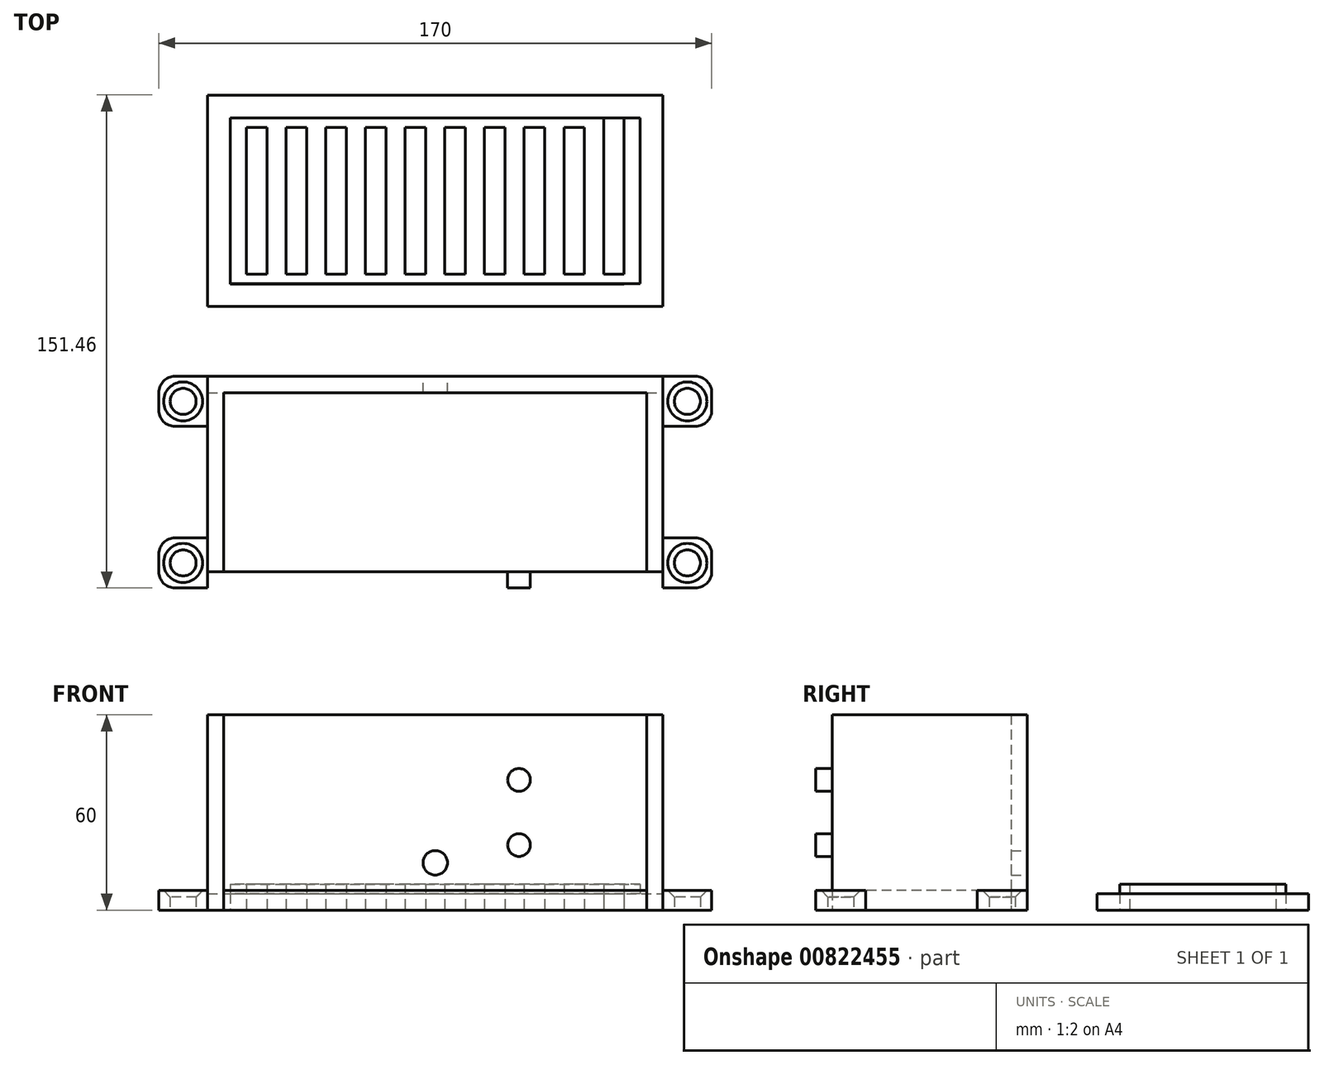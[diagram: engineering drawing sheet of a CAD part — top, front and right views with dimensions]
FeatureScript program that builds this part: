
annotation { "Feature Type Name" : "Feature", "Feature Type Description" : "" }
export const myFeature = defineFeature(function(context is Context, id is Id, definition is map)
    precondition{}
    {
        {
            var Q0;
            Q0=qCreatedBy(makeId("Top.planeOp"),FACE);
            var sketch = newSketch(context, id + "F0", { "sketchPlane" : qUnion([Q0])});
            skLineSegment(sketch, "E0.bottom", {"start": v(-70, 32.5) * mm, "end": v(70, 32.5) * mm});
            skLineSegment(sketch, "E0.top", {"start": v(-70, -32.5) * mm, "end": v(70, -32.5) * mm});
            skLineSegment(sketch, "E0.left", {"start": v(-70, 32.5) * mm, "end": v(-70, -32.5) * mm});
            skLineSegment(sketch, "E0.right", {"start": v(70, 32.5) * mm, "end": v(70, -32.5) * mm});
            skPoint(sketch, "E0.middle", {"position": v(0, 0) * mm});
            skLineSegment(sketch, "E1", {"start": v(70, -32.5) * mm, "end": v(80, -32.5) * mm});
            skCircle(sketch, "E2", {"center": v(77.5, -24.82) * mm, "radius": 4 * mm});
            skLineSegment(sketch, "E3", {"start": v(85, -27.5) * mm, "end": v(85, -22.13) * mm});
            skLineSegment(sketch, "E4", {"start": v(80, -17.13) * mm, "end": v(70, -17.13) * mm});
            skLineSegment(sketch, "E5", {"start": v(77.5, -32.5) * mm, "end": v(77.5, -17.13) * mm, "construction": true});
            skLineSegment(sketch, "E6", {"start": v(85, -24.82) * mm, "end": v(70, -24.82) * mm, "construction": true});
            skLineSegment(sketch, "E7.MirrorCS", {"start": v(80, 17.13) * mm, "end": v(70, 17.13) * mm});
            skCircle(sketch, "E8.MirrorC", {"center": v(77.5, 24.82) * mm, "radius": 4 * mm});
            skLineSegment(sketch, "E9.MirrorCS", {"start": v(85, 27.5) * mm, "end": v(85, 22.13) * mm});
            skLineSegment(sketch, "E10.MirrorCS", {"start": v(70, 32.5) * mm, "end": v(80, 32.5) * mm});
            skLineSegment(sketch, "E11.MirrorCS", {"start": v(-70, 32.5) * mm, "end": v(-80, 32.5) * mm});
            skLineSegment(sketch, "E12.MirrorCS", {"start": v(-80, 17.13) * mm, "end": v(-70, 17.13) * mm});
            skLineSegment(sketch, "E13.MirrorCS", {"start": v(-85, 27.5) * mm, "end": v(-85, 22.13) * mm});
            skCircle(sketch, "E14.MirrorC", {"center": v(-77.5, 24.82) * mm, "radius": 4 * mm});
            skLineSegment(sketch, "E15.MirrorCS", {"start": v(-80, -17.13) * mm, "end": v(-70, -17.13) * mm});
            skLineSegment(sketch, "E16.MirrorCS", {"start": v(-85, -27.5) * mm, "end": v(-85, -22.13) * mm});
            skLineSegment(sketch, "E17.MirrorCS", {"start": v(-70, -32.5) * mm, "end": v(-80, -32.5) * mm});
            skCircle(sketch, "E18.MirrorC", {"center": v(-77.5, -24.82) * mm, "radius": 4 * mm});
            skPoint(sketch, "E19.visualSharp", {"position": v(85, -17.13) * mm});
            skArc(sketch, "E19.filletArc", {"start": v(85, -22.13) * mm, "mid": v(83.54, -18.6) * mm, "end": v(80, -17.13) * mm});
            skPoint(sketch, "E20.visualSharp", {"position": v(85, -32.5) * mm});
            skArc(sketch, "E20.filletArc", {"start": v(80, -32.5) * mm, "mid": v(83.54, -31.04) * mm, "end": v(85, -27.5) * mm});
            skPoint(sketch, "E21.visualSharp", {"position": v(85, 32.5) * mm});
            skArc(sketch, "E21.filletArc", {"start": v(85, 27.5) * mm, "mid": v(83.54, 31.04) * mm, "end": v(80, 32.5) * mm});
            skPoint(sketch, "E22.visualSharp", {"position": v(85, 17.13) * mm});
            skArc(sketch, "E22.filletArc", {"start": v(80, 17.13) * mm, "mid": v(83.54, 18.6) * mm, "end": v(85, 22.13) * mm});
            skPoint(sketch, "E23.visualSharp", {"position": v(-85, 32.5) * mm});
            skArc(sketch, "E23.filletArc", {"start": v(-80, 32.5) * mm, "mid": v(-83.54, 31.04) * mm, "end": v(-85, 27.5) * mm});
            skPoint(sketch, "E24.visualSharp", {"position": v(-85, 17.13) * mm});
            skArc(sketch, "E24.filletArc", {"start": v(-85, 22.13) * mm, "mid": v(-83.54, 18.6) * mm, "end": v(-80, 17.13) * mm});
            skPoint(sketch, "E25.visualSharp", {"position": v(-85, -17.13) * mm});
            skArc(sketch, "E25.filletArc", {"start": v(-80, -17.13) * mm, "mid": v(-83.54, -18.6) * mm, "end": v(-85, -22.13) * mm});
            skPoint(sketch, "E26.visualSharp", {"position": v(-85, -32.5) * mm});
            skArc(sketch, "E26.filletArc", {"start": v(-85, -27.5) * mm, "mid": v(-83.54, -31.04) * mm, "end": v(-80, -32.5) * mm});
            skLineSegment(sketch, "E27", {"start": v(-65, 32.5) * mm, "end": v(-65, -32.5) * mm});
            skLineSegment(sketch, "E28", {"start": v(-70, 27.5) * mm, "end": v(70, 27.5) * mm});
            skLineSegment(sketch, "E29", {"start": v(65, 32.5) * mm, "end": v(65, -32.5) * mm});
            skLineSegment(sketch, "E30", {"start": v(-70, -27.5) * mm, "end": v(70, -27.5) * mm});
            skLineSegment(sketch, "E31.bottom", {"start": v(-70, 118.96) * mm, "end": v(70, 118.96) * mm});
            skLineSegment(sketch, "E31.top", {"start": v(-70, 53.96) * mm, "end": v(70, 53.96) * mm});
            skLineSegment(sketch, "E31.left", {"start": v(-70, 118.96) * mm, "end": v(-70, 53.96) * mm});
            skLineSegment(sketch, "E31.right", {"start": v(70, 118.96) * mm, "end": v(70, 53.96) * mm});
            skPoint(sketch, "E31.middle", {"position": v(0, 86.46) * mm});
            skPoint(sketch, "E31.middle.positionSnap0", {"position": v(0, -32.5) * mm});
            skPoint(sketch, "E31.centerSnap0", {"position": v(0, -32.5) * mm});
            skLineSegment(sketch, "E32", {"start": v(-63, 118.96) * mm, "end": v(-63, 53.96) * mm});
            skLineSegment(sketch, "E33", {"start": v(-70, 60.96) * mm, "end": v(70, 60.96) * mm});
            skLineSegment(sketch, "E34", {"start": v(63, 53.96) * mm, "end": v(63, 118.96) * mm});
            skLineSegment(sketch, "E35.top", {"start": v(-63, 60.91) * mm, "end": v(61.3, 60.91) * mm});
            skLineSegment(sketch, "E35.left", {"start": v(-63, 112.53) * mm, "end": v(-63, 60.91) * mm});
            skLineSegment(sketch, "E36", {"start": v(70, 111.96) * mm, "end": v(-70, 111.96) * mm});
            skLineSegment(sketch, "E37.bottom", {"start": v(58.04, 111.96) * mm, "end": v(51.74, 111.96) * mm});
            skLineSegment(sketch, "E37.top", {"start": v(58.04, 60.91) * mm, "end": v(51.74, 60.91) * mm});
            skLineSegment(sketch, "E37.left", {"start": v(58.04, 111.96) * mm, "end": v(58.04, 60.91) * mm});
            skLineSegment(sketch, "E37.right", {"start": v(51.74, 111.96) * mm, "end": v(51.74, 60.91) * mm});
            skLineSegment(sketch, "E38.1.0.0", {"start": v(39.54, 111.96) * mm, "end": v(39.54, 60.91) * mm});
            skLineSegment(sketch, "E38.1.0.1", {"start": v(45.84, 111.96) * mm, "end": v(45.84, 60.91) * mm});
            skLineSegment(sketch, "E38.2.0.0", {"start": v(27.34, 111.96) * mm, "end": v(27.34, 60.91) * mm});
            skLineSegment(sketch, "E38.2.0.1", {"start": v(33.64, 111.96) * mm, "end": v(33.64, 60.91) * mm});
            skLineSegment(sketch, "E38.direction1", {"start": v(51.74, 60.91) * mm, "end": v(39.54, 60.91) * mm, "construction": true});
            skLineSegment(sketch, "E39.0.3.0", {"start": v(15.14, 111.96) * mm, "end": v(15.14, 60.91) * mm});
            skLineSegment(sketch, "E39.3.3.0", {"start": v(21.44, 111.96) * mm, "end": v(21.44, 60.91) * mm});
            skLineSegment(sketch, "E39.0.4.0", {"start": v(2.94, 111.96) * mm, "end": v(2.94, 60.91) * mm});
            skLineSegment(sketch, "E39.3.4.0", {"start": v(9.24, 111.96) * mm, "end": v(9.24, 60.91) * mm});
            skLineSegment(sketch, "E39.0.5.0", {"start": v(-9.26, 111.96) * mm, "end": v(-9.26, 60.91) * mm});
            skLineSegment(sketch, "E39.3.5.0", {"start": v(-2.96, 111.96) * mm, "end": v(-2.96, 60.91) * mm});
            skLineSegment(sketch, "E39.0.6.0", {"start": v(-21.46, 111.96) * mm, "end": v(-21.46, 60.91) * mm});
            skLineSegment(sketch, "E39.3.6.0", {"start": v(-15.16, 111.96) * mm, "end": v(-15.16, 60.91) * mm});
            skLineSegment(sketch, "E39.0.7.0", {"start": v(-33.66, 111.96) * mm, "end": v(-33.66, 60.91) * mm});
            skLineSegment(sketch, "E39.3.7.0", {"start": v(-27.36, 111.96) * mm, "end": v(-27.36, 60.91) * mm});
            skLineSegment(sketch, "E39.0.8.0", {"start": v(-45.86, 111.96) * mm, "end": v(-45.86, 60.91) * mm});
            skLineSegment(sketch, "E39.3.8.0", {"start": v(-39.56, 111.96) * mm, "end": v(-39.56, 60.91) * mm});
            skLineSegment(sketch, "E39.0.9.0", {"start": v(-58.06, 111.96) * mm, "end": v(-58.06, 60.91) * mm});
            skLineSegment(sketch, "E39.3.9.0", {"start": v(-51.76, 111.96) * mm, "end": v(-51.76, 60.91) * mm});
            skLineSegment(sketch, "E40.bottom", {"start": v(-60, 108.96) * mm, "end": v(60, 108.96) * mm});
            skLineSegment(sketch, "E40.top", {"start": v(-60, 63.96) * mm, "end": v(60, 63.96) * mm});
            skLineSegment(sketch, "E40.left", {"start": v(-60, 108.96) * mm, "end": v(-60, 63.96) * mm});
            skLineSegment(sketch, "E40.right", {"start": v(60, 108.96) * mm, "end": v(60, 63.96) * mm});
            skSolve(sketch);
        }
        {
            var Q0;
            {var subQ2=sQuery(id+"F0.wireOp",EDGE,"E11.MirrorCS");Q0=makeQuery(id+"F0.imprint","IMPRINT",FACE,{"disambiguationData":[TD([[makeQuery(id+"F0.imprint","IMPRINT",EDGE,{"derivedFrom":subQ2}),1.0]])]});}
            var Q1;
            {var subQ1=sQuery(id+"F0.wireOp",EDGE,"E15.MirrorCS");Q1=makeQuery(id+"F0.imprint","IMPRINT",FACE,{"disambiguationData":[TD([[makeQuery(id+"F0.imprint","IMPRINT",EDGE,{"derivedFrom":subQ1}),-1.0]])]});}
            var Q2;
            {var subQ4=sQuery(id+"F0.wireOp",EDGE,"E0.bottom");Q2=makeQuery(id+"F0.imprint","IMPRINT",FACE,{"disambiguationData":[TD([[makeQuery(id+"F0.imprint","IMPRINT",EDGE,{"derivedFrom":subQ4}),-1.0]])]});}
            var Q3;
            {var subQ0=sQuery(id+"F0.wireOp",EDGE,"E1");Q3=makeQuery(id+"F0.imprint","IMPRINT",FACE,{"disambiguationData":[TD([[makeQuery(id+"F0.imprint","IMPRINT",EDGE,{"derivedFrom":subQ0}),1.0]])]});}
            var Q4;
            {var subQ0=sQuery(id+"F0.wireOp",EDGE,"E7.MirrorCS");Q4=makeQuery(id+"F0.imprint","IMPRINT",FACE,{"disambiguationData":[TD([[makeQuery(id+"F0.imprint","IMPRINT",EDGE,{"derivedFrom":subQ0}),-1.0]])]});}
            extrude(context, id + "F1", {"entities" : qUnion([Q0, Q1, Q2, Q3, Q4]), "depth" : 6 * mm, "offsetDistance" : 25 * mm});
        }
        {
            var Q0;
            Q0=makeQuery(id+"F1.opExtrude","CAP_EDGE",EDGE,{"disambiguationData":[OSD([sQuery(id+"F0.wireOp",EDGE,"E14.MirrorC")])],"isStart":false});
            var Q1;
            Q1=makeQuery(id+"F1.opExtrude","CAP_EDGE",EDGE,{"disambiguationData":[OSD([sQuery(id+"F0.wireOp",EDGE,"E18.MirrorC")])],"isStart":false});
            var Q2;
            Q2=makeQuery(id+"F1.opExtrude","CAP_EDGE",EDGE,{"disambiguationData":[OSD([sQuery(id+"F0.wireOp",EDGE,"E2")])],"isStart":false});
            var Q3;
            Q3=makeQuery(id+"F1.opExtrude","CAP_EDGE",EDGE,{"disambiguationData":[OSD([sQuery(id+"F0.wireOp",EDGE,"E8.MirrorC")])],"isStart":false});
            chamfer(context, id + "F2", {"entities" : qUnion([Q0, Q1, Q2, Q3]), "width" : 2 * mm, "tangentPropagation" : true});
        }
        {
            var Q0;
            {var subQ0=sQuery(id+"F0.wireOp",EDGE,"E0.left");var subQ4=makeQuery(id+"F0.imprint","INTERSECT",VERTEX,{"derivedFrom":[subQ0,sQuery(id+"F0.wireOp",EDGE,"E12.MirrorCS")]});Q0=makeQuery(id+"F0.imprint","IMPRINT",FACE,{"disambiguationData":[TD([[makeQuery(id+"F0.imprint","IMPRINT",EDGE,{"disambiguationData":[TD([[subQ4,1.0]])],"derivedFrom":subQ0}),1.0]])]});}
            var Q1;
            {var subQ0=sQuery(id+"F0.wireOp",EDGE,"E27");var subQ1=sQuery(id+"F0.wireOp",EDGE,"E0.top");var subQ2=makeQuery(id+"F0.imprint","INTERSECT",VERTEX,{"derivedFrom":[subQ1,subQ0]});Q1=makeQuery(id+"F0.imprint","IMPRINT",FACE,{"disambiguationData":[TD([[makeQuery(id+"F0.imprint","IMPRINT",EDGE,{"disambiguationData":[TD([[subQ2,-1.0]])],"derivedFrom":subQ1}),1.0]])]});}
            var Q2;
            {var subQ1=sQuery(id+"F0.wireOp",EDGE,"E0.top");var subQ3=sQuery(id+"F0.wireOp",EDGE,"E27");var subQ4=makeQuery(id+"F0.imprint","INTERSECT",VERTEX,{"derivedFrom":[subQ1,subQ3]});Q2=makeQuery(id+"F0.imprint","IMPRINT",FACE,{"disambiguationData":[TD([[makeQuery(id+"F0.imprint","IMPRINT",EDGE,{"disambiguationData":[TD([[subQ4,1.0]])],"derivedFrom":subQ3}),-1.0]])]});}
            var Q3;
            {var subQ1=sQuery(id+"F0.wireOp",EDGE,"E0.top");var subQ3=sQuery(id+"F0.wireOp",EDGE,"E29");var subQ4=makeQuery(id+"F0.imprint","INTERSECT",VERTEX,{"derivedFrom":[subQ1,subQ3]});Q3=makeQuery(id+"F0.imprint","IMPRINT",FACE,{"disambiguationData":[TD([[makeQuery(id+"F0.imprint","IMPRINT",EDGE,{"disambiguationData":[TD([[subQ4,1.0]])],"derivedFrom":subQ3}),1.0]])]});}
            var Q4;
            {var subQ1=sQuery(id+"F0.wireOp",EDGE,"E0.right");var subQ8=makeQuery(id+"F0.imprint","INTERSECT",VERTEX,{"derivedFrom":[subQ1,sQuery(id+"F0.wireOp",EDGE,"E7.MirrorCS")]});Q4=makeQuery(id+"F0.imprint","IMPRINT",FACE,{"disambiguationData":[TD([[makeQuery(id+"F0.imprint","IMPRINT",EDGE,{"disambiguationData":[TD([[subQ8,1.0]])],"derivedFrom":subQ1}),-1.0]])]});}
            var Q5;
            {var subQ0=sQuery(id+"F0.wireOp",EDGE,"E0.right");var subQ5=sQuery(id+"F0.wireOp",EDGE,"E28");var subQ6=makeQuery(id+"F0.imprint","INTERSECT",VERTEX,{"derivedFrom":[subQ0,subQ5]});Q5=makeQuery(id+"F0.imprint","IMPRINT",FACE,{"disambiguationData":[TD([[makeQuery(id+"F0.imprint","IMPRINT",EDGE,{"disambiguationData":[TD([[subQ6,1.0]])],"derivedFrom":subQ5}),1.0]])]});}
            var Q6;
            {var subQ0=sQuery(id+"F0.wireOp",EDGE,"E27");var subQ1=sQuery(id+"F0.wireOp",EDGE,"E0.bottom");var subQ2=makeQuery(id+"F0.imprint","INTERSECT",VERTEX,{"derivedFrom":[subQ1,subQ0]});Q6=makeQuery(id+"F0.imprint","IMPRINT",FACE,{"disambiguationData":[TD([[makeQuery(id+"F0.imprint","IMPRINT",EDGE,{"disambiguationData":[TD([[subQ2,-1.0]])],"derivedFrom":subQ1}),-1.0]])]});}
            var Q7;
            {var subQ1=sQuery(id+"F0.wireOp",EDGE,"E0.bottom");var subQ3=sQuery(id+"F0.wireOp",EDGE,"E27");var subQ4=makeQuery(id+"F0.imprint","INTERSECT",VERTEX,{"derivedFrom":[subQ1,subQ3]});Q7=makeQuery(id+"F0.imprint","IMPRINT",FACE,{"disambiguationData":[TD([[makeQuery(id+"F0.imprint","IMPRINT",EDGE,{"disambiguationData":[TD([[subQ4,-1.0]])],"derivedFrom":subQ3}),-1.0]])]});}
            extrude(context, id + "F3", {"entities" : qUnion([Q0, Q1, Q2, Q3, Q4, Q5, Q6, Q7]), "depth" : 60 * mm, "offsetDistance" : 25 * mm});
        }
        {
            var Q0;
            {var subQ0=sQuery(id+"F0.wireOp",EDGE,"E28");var subQ1=sQuery(id+"F0.wireOp",EDGE,"E27");var subQ2=makeQuery(id+"F0.imprint","INTERSECT",VERTEX,{"derivedFrom":[subQ1,subQ0]});Q0=makeQuery(id+"F0.imprint","IMPRINT",FACE,{"disambiguationData":[TD([[makeQuery(id+"F0.imprint","IMPRINT",EDGE,{"disambiguationData":[TD([[subQ2,-1.0]])],"derivedFrom":subQ1}),1.0]])]});}
            extrude(context, id + "F4", {"entities" : qUnion([Q0]), "depth" : 6 * mm, "offsetDistance" : 25 * mm});
        }
        {
            var Q0;
            Q0=makeQuery(id+"F3.opExtrude","SWEPT_FACE",FACE,{"disambiguationData":[OSD([sQuery(id+"F0.wireOp",EDGE,"E0.top")])]});
            var sketch = newSketch(context, id + "F5", { "sketchPlane" : qUnion([Q0])});
            skLineSegment(sketch, "E41.bottom", {"start": v(-12, 20) * mm, "end": v(-58, 20) * mm});
            skLineSegment(sketch, "E41.top", {"start": v(-12, 50) * mm, "end": v(-58, 50) * mm});
            skLineSegment(sketch, "E41.left", {"start": v(-12, 20) * mm, "end": v(-12, 50) * mm});
            skLineSegment(sketch, "E41.right", {"start": v(-58, 20) * mm, "end": v(-58, 50) * mm});
            skPoint(sketch, "E41.middle", {"position": v(-35, 35) * mm});
            skLineSegment(sketch, "E42", {"start": v(-70, 60) * mm, "end": v(-70, 35) * mm});
            skLineSegment(sketch, "E43", {"start": v(-70, 60) * mm, "end": v(-35, 60) * mm});
            skLineSegment(sketch, "E44", {"start": v(-70, 35) * mm, "end": v(-35, 35) * mm, "construction": true});
            skLineSegment(sketch, "E45", {"start": v(-35, 35) * mm, "end": v(-35, 60) * mm, "construction": true});
            skLineSegment(sketch, "E46", {"start": v(0, 60) * mm, "end": v(70, 60) * mm});
            skLineSegment(sketch, "E47", {"start": v(0, 0) * mm, "end": v(70, 0) * mm});
            skLineSegment(sketch, "E48", {"start": v(35, 60) * mm, "end": v(35, 0) * mm, "construction": true});
            skLineSegment(sketch, "E49", {"start": v(35, 60) * mm, "end": v(35, 40) * mm});
            skLineSegment(sketch, "E50", {"start": v(35, 0) * mm, "end": v(35, 20) * mm});
            skLineSegment(sketch, "E51", {"start": v(35, 40) * mm, "end": v(44.25, 40) * mm});
            skLineSegment(sketch, "E52", {"start": v(35, 20) * mm, "end": v(44.25, 20) * mm});
            skCircle(sketch, "E53", {"center": v(44.25, 40) * mm, "radius": 3.5 * mm});
            skCircle(sketch, "E54", {"center": v(44.25, 20) * mm, "radius": 3.5 * mm});
            skLineSegment(sketch, "E55.MirrorCS", {"start": v(35, 40) * mm, "end": v(25.75, 40) * mm});
            skCircle(sketch, "E56.MirrorC", {"center": v(25.75, 40) * mm, "radius": 3.5 * mm});
            skLineSegment(sketch, "E57.MirrorCS", {"start": v(35, 20) * mm, "end": v(25.75, 20) * mm});
            skCircle(sketch, "E58.MirrorC", {"center": v(25.75, 20) * mm, "radius": 3.5 * mm});
            skSolve(sketch);
        }
        {
            var Q0;
            Q0=makeQuery(id+"F5.imprint","IMPRINT",FACE,{"disambiguationData":[TD([[makeQuery(id+"F5.imprint","IMPRINT",EDGE,{"derivedFrom":sQuery(id+"F5.wireOp",EDGE,"E41.bottom")}),-1.0]])]});
            var Q1;
            Q1=makeQuery(id+"F5.imprint","IMPRINT",FACE,{"disambiguationData":[TD([[makeQuery(id+"F5.imprint","IMPRINT",EDGE,{"derivedFrom":sQuery(id+"F5.wireOp",EDGE,"E56.MirrorC")}),-1.0]])]});
            var Q2;
            Q2=makeQuery(id+"F5.imprint","IMPRINT",FACE,{"disambiguationData":[TD([[makeQuery(id+"F5.imprint","IMPRINT",EDGE,{"derivedFrom":sQuery(id+"F5.wireOp",EDGE,"E58.MirrorC")}),-1.0]])]});
            var Q3;
            Q3=makeQuery(id+"F5.imprint","IMPRINT",FACE,{"disambiguationData":[TD([[makeQuery(id+"F5.imprint","IMPRINT",EDGE,{"derivedFrom":sQuery(id+"F5.wireOp",EDGE,"E53")}),1.0]])]});
            var Q4;
            Q4=makeQuery(id+"F5.imprint","IMPRINT",FACE,{"disambiguationData":[TD([[makeQuery(id+"F5.imprint","IMPRINT",EDGE,{"derivedFrom":sQuery(id+"F5.wireOp",EDGE,"E54")}),1.0]])]});
            extrude(context, id + "F6", {"entities" : qUnion([Q0, Q1, Q2, Q3, Q4]), "operationType" : NewBodyOperationType.REMOVE, "oppositeDirection" : true, "depth" : 5 * mm, "offsetDistance" : 25 * mm});
        }
        {
            var Q0;
            Q0=makeQuery(id+"F3.opExtrude","SWEPT_FACE",FACE,{"disambiguationData":[OSD([sQuery(id+"F0.wireOp",EDGE,"E0.bottom")])]});
            var sketch = newSketch(context, id + "F7", { "sketchPlane" : qUnion([Q0])});
            skCircle(sketch, "E59", {"center": v(0, 14.53) * mm, "radius": 3.75 * mm});
            skSolve(sketch);
        }
        {
            var Q0;
            Q0=makeQuery(id+"F7.imprint","IMPRINT",FACE,{"disambiguationData":[TD([[makeQuery(id+"F7.imprint","IMPRINT",EDGE,{"derivedFrom":sQuery(id+"F7.wireOp",EDGE,"E59")}),1.0]])]});
            extrude(context, id + "F8", {"entities" : qUnion([Q0]), "operationType" : NewBodyOperationType.REMOVE, "oppositeDirection" : true, "depth" : 5 * mm, "offsetDistance" : 25 * mm});
        }
        {
            var Q0;
            {var subQ0=sQuery(id+"F0.wireOp",EDGE,"E31.right");var subQ1=sQuery(id+"F0.wireOp",EDGE,"E31.bottom");var subQ2=makeQuery(id+"F0.imprint","INTERSECT",VERTEX,{"derivedFrom":[subQ1,subQ0]});Q0=makeQuery(id+"F0.imprint","IMPRINT",FACE,{"disambiguationData":[TD([[makeQuery(id+"F0.imprint","IMPRINT",EDGE,{"disambiguationData":[TD([[subQ2,1.0]])],"derivedFrom":subQ1}),-1.0]])]});}
            var Q1;
            {var subQ2=sQuery(id+"F0.wireOp",EDGE,"E32");var subQ13=sQuery(id+"F0.wireOp",EDGE,"E31.bottom");var subQ14=makeQuery(id+"F0.imprint","INTERSECT",VERTEX,{"derivedFrom":[subQ13,subQ2]});Q1=makeQuery(id+"F0.imprint","IMPRINT",FACE,{"disambiguationData":[TD([[makeQuery(id+"F0.imprint","IMPRINT",EDGE,{"disambiguationData":[TD([[subQ14,-1.0]])],"derivedFrom":subQ13}),-1.0]])]});}
            var Q2;
            {var subQ9=sQuery(id+"F0.wireOp",EDGE,"E33");var subQ10=sQuery(id+"F0.wireOp",EDGE,"E31.right");var subQ11=makeQuery(id+"F0.imprint","INTERSECT",VERTEX,{"derivedFrom":[subQ10,subQ9]});Q2=makeQuery(id+"F0.imprint","IMPRINT",FACE,{"disambiguationData":[TD([[makeQuery(id+"F0.imprint","IMPRINT",EDGE,{"disambiguationData":[TD([[subQ11,1.0]])],"derivedFrom":subQ10}),-1.0]])]});}
            var Q3;
            {var subQ0=sQuery(id+"F0.wireOp",EDGE,"E31.right");var subQ1=sQuery(id+"F0.wireOp",EDGE,"E31.top");var subQ2=makeQuery(id+"F0.imprint","INTERSECT",VERTEX,{"derivedFrom":[subQ1,subQ0]});Q3=makeQuery(id+"F0.imprint","IMPRINT",FACE,{"disambiguationData":[TD([[makeQuery(id+"F0.imprint","IMPRINT",EDGE,{"disambiguationData":[TD([[subQ2,1.0]])],"derivedFrom":subQ1}),1.0]])]});}
            var Q4;
            {var subQ6=sQuery(id+"F0.wireOp",EDGE,"E32");var subQ7=sQuery(id+"F0.wireOp",EDGE,"E31.top");var subQ8=makeQuery(id+"F0.imprint","INTERSECT",VERTEX,{"derivedFrom":[subQ7,subQ6]});Q4=makeQuery(id+"F0.imprint","IMPRINT",FACE,{"disambiguationData":[TD([[makeQuery(id+"F0.imprint","IMPRINT",EDGE,{"disambiguationData":[TD([[subQ8,-1.0]])],"derivedFrom":subQ7}),1.0]])]});}
            var Q5;
            {var subQ0=sQuery(id+"F0.wireOp",EDGE,"E31.left");var subQ1=sQuery(id+"F0.wireOp",EDGE,"E31.top");var subQ2=makeQuery(id+"F0.imprint","INTERSECT",VERTEX,{"derivedFrom":[subQ1,subQ0]});Q5=makeQuery(id+"F0.imprint","IMPRINT",FACE,{"disambiguationData":[TD([[makeQuery(id+"F0.imprint","IMPRINT",EDGE,{"disambiguationData":[TD([[subQ2,-1.0]])],"derivedFrom":subQ1}),1.0]])]});}
            var Q6;
            {var subQ0=sQuery(id+"F0.wireOp",EDGE,"E33");var subQ1=sQuery(id+"F0.wireOp",EDGE,"E31.left");var subQ2=makeQuery(id+"F0.imprint","INTERSECT",VERTEX,{"derivedFrom":[subQ1,subQ0]});Q6=makeQuery(id+"F0.imprint","IMPRINT",FACE,{"disambiguationData":[TD([[makeQuery(id+"F0.imprint","IMPRINT",EDGE,{"disambiguationData":[TD([[subQ2,1.0]])],"derivedFrom":subQ1}),1.0]])]});}
            var Q7;
            {var subQ0=sQuery(id+"F0.wireOp",EDGE,"E31.left");var subQ1=sQuery(id+"F0.wireOp",EDGE,"E31.bottom");var subQ2=makeQuery(id+"F0.imprint","INTERSECT",VERTEX,{"derivedFrom":[subQ1,subQ0]});Q7=makeQuery(id+"F0.imprint","IMPRINT",FACE,{"disambiguationData":[TD([[makeQuery(id+"F0.imprint","IMPRINT",EDGE,{"disambiguationData":[TD([[subQ2,-1.0]])],"derivedFrom":subQ1}),-1.0]])]});}
            extrude(context, id + "F9", {"entities" : qUnion([Q0, Q1, Q2, Q3, Q4, Q5, Q6, Q7]), "depth" : 5 * mm, "offsetDistance" : 25 * mm});
        }
        {
            var Q0;
            {var subQ0=sQuery(id+"F0.wireOp",EDGE,"E40.bottom");var subQ1=sQuery(id+"F0.wireOp",EDGE,"E39.0.9.0");var subQ2=makeQuery(id+"F0.imprint","INTERSECT",VERTEX,{"derivedFrom":[subQ1,subQ0]});Q0=makeQuery(id+"F0.imprint","IMPRINT",FACE,{"disambiguationData":[TD([[makeQuery(id+"F0.imprint","IMPRINT",EDGE,{"disambiguationData":[TD([[subQ2,-1.0]])],"derivedFrom":subQ1}),1.0]])]});}
            var Q1;
            {var subQ0=sQuery(id+"F0.wireOp",EDGE,"E40.bottom");var subQ1=sQuery(id+"F0.wireOp",EDGE,"E39.0.8.0");var subQ2=makeQuery(id+"F0.imprint","INTERSECT",VERTEX,{"derivedFrom":[subQ1,subQ0]});Q1=makeQuery(id+"F0.imprint","IMPRINT",FACE,{"disambiguationData":[TD([[makeQuery(id+"F0.imprint","IMPRINT",EDGE,{"disambiguationData":[TD([[subQ2,-1.0]])],"derivedFrom":subQ1}),-1.0]])]});}
            var Q2;
            {var subQ0=sQuery(id+"F0.wireOp",EDGE,"E40.bottom");var subQ1=sQuery(id+"F0.wireOp",EDGE,"E39.0.8.0");var subQ2=makeQuery(id+"F0.imprint","INTERSECT",VERTEX,{"derivedFrom":[subQ1,subQ0]});Q2=makeQuery(id+"F0.imprint","IMPRINT",FACE,{"disambiguationData":[TD([[makeQuery(id+"F0.imprint","IMPRINT",EDGE,{"disambiguationData":[TD([[subQ2,-1.0]])],"derivedFrom":subQ1}),1.0]])]});}
            var Q3;
            {var subQ0=sQuery(id+"F0.wireOp",EDGE,"E40.bottom");var subQ1=sQuery(id+"F0.wireOp",EDGE,"E39.0.7.0");var subQ2=makeQuery(id+"F0.imprint","INTERSECT",VERTEX,{"derivedFrom":[subQ1,subQ0]});Q3=makeQuery(id+"F0.imprint","IMPRINT",FACE,{"disambiguationData":[TD([[makeQuery(id+"F0.imprint","IMPRINT",EDGE,{"disambiguationData":[TD([[subQ2,-1.0]])],"derivedFrom":subQ1}),-1.0]])]});}
            var Q4;
            {var subQ0=sQuery(id+"F0.wireOp",EDGE,"E40.bottom");var subQ1=sQuery(id+"F0.wireOp",EDGE,"E39.0.7.0");var subQ2=makeQuery(id+"F0.imprint","INTERSECT",VERTEX,{"derivedFrom":[subQ1,subQ0]});Q4=makeQuery(id+"F0.imprint","IMPRINT",FACE,{"disambiguationData":[TD([[makeQuery(id+"F0.imprint","IMPRINT",EDGE,{"disambiguationData":[TD([[subQ2,-1.0]])],"derivedFrom":subQ1}),1.0]])]});}
            var Q5;
            {var subQ0=sQuery(id+"F0.wireOp",EDGE,"E40.bottom");var subQ1=sQuery(id+"F0.wireOp",EDGE,"E39.0.6.0");var subQ2=makeQuery(id+"F0.imprint","INTERSECT",VERTEX,{"derivedFrom":[subQ1,subQ0]});Q5=makeQuery(id+"F0.imprint","IMPRINT",FACE,{"disambiguationData":[TD([[makeQuery(id+"F0.imprint","IMPRINT",EDGE,{"disambiguationData":[TD([[subQ2,-1.0]])],"derivedFrom":subQ1}),-1.0]])]});}
            var Q6;
            {var subQ0=sQuery(id+"F0.wireOp",EDGE,"E40.bottom");var subQ1=sQuery(id+"F0.wireOp",EDGE,"E39.0.6.0");var subQ2=makeQuery(id+"F0.imprint","INTERSECT",VERTEX,{"derivedFrom":[subQ1,subQ0]});Q6=makeQuery(id+"F0.imprint","IMPRINT",FACE,{"disambiguationData":[TD([[makeQuery(id+"F0.imprint","IMPRINT",EDGE,{"disambiguationData":[TD([[subQ2,-1.0]])],"derivedFrom":subQ1}),1.0]])]});}
            var Q7;
            {var subQ0=sQuery(id+"F0.wireOp",EDGE,"E40.bottom");var subQ1=sQuery(id+"F0.wireOp",EDGE,"E39.0.5.0");var subQ2=makeQuery(id+"F0.imprint","INTERSECT",VERTEX,{"derivedFrom":[subQ1,subQ0]});Q7=makeQuery(id+"F0.imprint","IMPRINT",FACE,{"disambiguationData":[TD([[makeQuery(id+"F0.imprint","IMPRINT",EDGE,{"disambiguationData":[TD([[subQ2,-1.0]])],"derivedFrom":subQ1}),-1.0]])]});}
            var Q8;
            {var subQ0=sQuery(id+"F0.wireOp",EDGE,"E40.bottom");var subQ1=sQuery(id+"F0.wireOp",EDGE,"E39.0.5.0");var subQ2=makeQuery(id+"F0.imprint","INTERSECT",VERTEX,{"derivedFrom":[subQ1,subQ0]});Q8=makeQuery(id+"F0.imprint","IMPRINT",FACE,{"disambiguationData":[TD([[makeQuery(id+"F0.imprint","IMPRINT",EDGE,{"disambiguationData":[TD([[subQ2,-1.0]])],"derivedFrom":subQ1}),1.0]])]});}
            var Q9;
            {var subQ0=sQuery(id+"F0.wireOp",EDGE,"E40.bottom");var subQ1=sQuery(id+"F0.wireOp",EDGE,"E39.0.4.0");var subQ2=makeQuery(id+"F0.imprint","INTERSECT",VERTEX,{"derivedFrom":[subQ1,subQ0]});Q9=makeQuery(id+"F0.imprint","IMPRINT",FACE,{"disambiguationData":[TD([[makeQuery(id+"F0.imprint","IMPRINT",EDGE,{"disambiguationData":[TD([[subQ2,-1.0]])],"derivedFrom":subQ1}),-1.0]])]});}
            var Q10;
            {var subQ0=sQuery(id+"F0.wireOp",EDGE,"E40.bottom");var subQ1=sQuery(id+"F0.wireOp",EDGE,"E39.0.4.0");var subQ2=makeQuery(id+"F0.imprint","INTERSECT",VERTEX,{"derivedFrom":[subQ1,subQ0]});Q10=makeQuery(id+"F0.imprint","IMPRINT",FACE,{"disambiguationData":[TD([[makeQuery(id+"F0.imprint","IMPRINT",EDGE,{"disambiguationData":[TD([[subQ2,-1.0]])],"derivedFrom":subQ1}),1.0]])]});}
            var Q11;
            {var subQ0=sQuery(id+"F0.wireOp",EDGE,"E40.bottom");var subQ1=sQuery(id+"F0.wireOp",EDGE,"E39.0.3.0");var subQ2=makeQuery(id+"F0.imprint","INTERSECT",VERTEX,{"derivedFrom":[subQ1,subQ0]});Q11=makeQuery(id+"F0.imprint","IMPRINT",FACE,{"disambiguationData":[TD([[makeQuery(id+"F0.imprint","IMPRINT",EDGE,{"disambiguationData":[TD([[subQ2,-1.0]])],"derivedFrom":subQ1}),-1.0]])]});}
            var Q12;
            {var subQ0=sQuery(id+"F0.wireOp",EDGE,"E40.bottom");var subQ1=sQuery(id+"F0.wireOp",EDGE,"E39.0.3.0");var subQ2=makeQuery(id+"F0.imprint","INTERSECT",VERTEX,{"derivedFrom":[subQ1,subQ0]});Q12=makeQuery(id+"F0.imprint","IMPRINT",FACE,{"disambiguationData":[TD([[makeQuery(id+"F0.imprint","IMPRINT",EDGE,{"disambiguationData":[TD([[subQ2,-1.0]])],"derivedFrom":subQ1}),1.0]])]});}
            var Q13;
            {var subQ0=sQuery(id+"F0.wireOp",EDGE,"E40.bottom");var subQ1=sQuery(id+"F0.wireOp",EDGE,"E38.2.0.0");var subQ2=makeQuery(id+"F0.imprint","INTERSECT",VERTEX,{"derivedFrom":[subQ1,subQ0]});Q13=makeQuery(id+"F0.imprint","IMPRINT",FACE,{"disambiguationData":[TD([[makeQuery(id+"F0.imprint","IMPRINT",EDGE,{"disambiguationData":[TD([[subQ2,-1.0]])],"derivedFrom":subQ1}),-1.0]])]});}
            var Q14;
            {var subQ0=sQuery(id+"F0.wireOp",EDGE,"E40.bottom");var subQ1=sQuery(id+"F0.wireOp",EDGE,"E38.2.0.0");var subQ2=makeQuery(id+"F0.imprint","INTERSECT",VERTEX,{"derivedFrom":[subQ1,subQ0]});Q14=makeQuery(id+"F0.imprint","IMPRINT",FACE,{"disambiguationData":[TD([[makeQuery(id+"F0.imprint","IMPRINT",EDGE,{"disambiguationData":[TD([[subQ2,-1.0]])],"derivedFrom":subQ1}),1.0]])]});}
            var Q15;
            {var subQ0=sQuery(id+"F0.wireOp",EDGE,"E40.bottom");var subQ1=sQuery(id+"F0.wireOp",EDGE,"E38.1.0.0");var subQ2=makeQuery(id+"F0.imprint","INTERSECT",VERTEX,{"derivedFrom":[subQ1,subQ0]});Q15=makeQuery(id+"F0.imprint","IMPRINT",FACE,{"disambiguationData":[TD([[makeQuery(id+"F0.imprint","IMPRINT",EDGE,{"disambiguationData":[TD([[subQ2,-1.0]])],"derivedFrom":subQ1}),-1.0]])]});}
            var Q16;
            {var subQ0=sQuery(id+"F0.wireOp",EDGE,"E40.bottom");var subQ1=sQuery(id+"F0.wireOp",EDGE,"E38.1.0.0");var subQ2=makeQuery(id+"F0.imprint","INTERSECT",VERTEX,{"derivedFrom":[subQ1,subQ0]});Q16=makeQuery(id+"F0.imprint","IMPRINT",FACE,{"disambiguationData":[TD([[makeQuery(id+"F0.imprint","IMPRINT",EDGE,{"disambiguationData":[TD([[subQ2,-1.0]])],"derivedFrom":subQ1}),1.0]])]});}
            var Q17;
            {var subQ0=sQuery(id+"F0.wireOp",EDGE,"E40.bottom");var subQ1=sQuery(id+"F0.wireOp",EDGE,"E37.right");var subQ2=makeQuery(id+"F0.imprint","INTERSECT",VERTEX,{"derivedFrom":[subQ1,subQ0]});Q17=makeQuery(id+"F0.imprint","IMPRINT",FACE,{"disambiguationData":[TD([[makeQuery(id+"F0.imprint","IMPRINT",EDGE,{"disambiguationData":[TD([[subQ2,-1.0]])],"derivedFrom":subQ1}),-1.0]])]});}
            var Q18;
            {var subQ0=sQuery(id+"F0.wireOp",EDGE,"E40.bottom");var subQ1=sQuery(id+"F0.wireOp",EDGE,"E37.left");var subQ2=makeQuery(id+"F0.imprint","INTERSECT",VERTEX,{"derivedFrom":[subQ1,subQ0]});Q18=makeQuery(id+"F0.imprint","IMPRINT",FACE,{"disambiguationData":[TD([[makeQuery(id+"F0.imprint","IMPRINT",EDGE,{"disambiguationData":[TD([[subQ2,-1.0]])],"derivedFrom":subQ1}),-1.0]])]});}
            var Q19;
            {var subQ5=sQuery(id+"F0.wireOp",EDGE,"E40.right");Q19=makeQuery(id+"F0.imprint","IMPRINT",FACE,{"disambiguationData":[TD([[makeQuery(id+"F0.imprint","IMPRINT",EDGE,{"derivedFrom":subQ5}),-1.0]])]});}
            var Q20;
            {var subQ5=sQuery(id+"F0.wireOp",EDGE,"E40.right");Q20=makeQuery(id+"F0.imprint","IMPRINT",FACE,{"disambiguationData":[TD([[makeQuery(id+"F0.imprint","IMPRINT",EDGE,{"derivedFrom":subQ5}),1.0]])]});}
            var Q21;
            {var subQ12=sQuery(id+"F0.wireOp",EDGE,"E40.left");Q21=makeQuery(id+"F0.imprint","IMPRINT",FACE,{"disambiguationData":[TD([[makeQuery(id+"F0.imprint","IMPRINT",EDGE,{"derivedFrom":subQ12}),-1.0]])]});}
            var Q22;
            {var subQ5=sQuery(id+"F0.wireOp",EDGE,"E40.left");Q22=makeQuery(id+"F0.imprint","IMPRINT",FACE,{"disambiguationData":[TD([[makeQuery(id+"F0.imprint","IMPRINT",EDGE,{"derivedFrom":subQ5}),1.0]])]});}
            var Q23;
            {var subQ0=sQuery(id+"F0.wireOp",EDGE,"E39.0.9.0");var subQ1=sQuery(id+"F0.wireOp",EDGE,"E33");var subQ2=makeQuery(id+"F0.imprint","INTERSECT",VERTEX,{"derivedFrom":[subQ1,subQ0]});Q23=makeQuery(id+"F0.imprint","IMPRINT",FACE,{"disambiguationData":[TD([[makeQuery(id+"F0.imprint","IMPRINT",EDGE,{"disambiguationData":[TD([[subQ2,-1.0]])],"derivedFrom":subQ1}),1.0]])]});}
            var Q24;
            {var subQ0=sQuery(id+"F0.wireOp",EDGE,"E39.3.9.0");var subQ1=sQuery(id+"F0.wireOp",EDGE,"E33");var subQ2=makeQuery(id+"F0.imprint","INTERSECT",VERTEX,{"derivedFrom":[subQ1,subQ0]});Q24=makeQuery(id+"F0.imprint","IMPRINT",FACE,{"disambiguationData":[TD([[makeQuery(id+"F0.imprint","IMPRINT",EDGE,{"disambiguationData":[TD([[subQ2,-1.0]])],"derivedFrom":subQ1}),1.0]])]});}
            var Q25;
            {var subQ0=sQuery(id+"F0.wireOp",EDGE,"E39.0.8.0");var subQ1=sQuery(id+"F0.wireOp",EDGE,"E33");var subQ2=makeQuery(id+"F0.imprint","INTERSECT",VERTEX,{"derivedFrom":[subQ1,subQ0]});Q25=makeQuery(id+"F0.imprint","IMPRINT",FACE,{"disambiguationData":[TD([[makeQuery(id+"F0.imprint","IMPRINT",EDGE,{"disambiguationData":[TD([[subQ2,-1.0]])],"derivedFrom":subQ1}),1.0]])]});}
            var Q26;
            {var subQ0=sQuery(id+"F0.wireOp",EDGE,"E39.3.8.0");var subQ1=sQuery(id+"F0.wireOp",EDGE,"E33");var subQ2=makeQuery(id+"F0.imprint","INTERSECT",VERTEX,{"derivedFrom":[subQ1,subQ0]});Q26=makeQuery(id+"F0.imprint","IMPRINT",FACE,{"disambiguationData":[TD([[makeQuery(id+"F0.imprint","IMPRINT",EDGE,{"disambiguationData":[TD([[subQ2,-1.0]])],"derivedFrom":subQ1}),1.0]])]});}
            var Q27;
            {var subQ0=sQuery(id+"F0.wireOp",EDGE,"E39.0.7.0");var subQ1=sQuery(id+"F0.wireOp",EDGE,"E33");var subQ2=makeQuery(id+"F0.imprint","INTERSECT",VERTEX,{"derivedFrom":[subQ1,subQ0]});Q27=makeQuery(id+"F0.imprint","IMPRINT",FACE,{"disambiguationData":[TD([[makeQuery(id+"F0.imprint","IMPRINT",EDGE,{"disambiguationData":[TD([[subQ2,-1.0]])],"derivedFrom":subQ1}),1.0]])]});}
            var Q28;
            {var subQ0=sQuery(id+"F0.wireOp",EDGE,"E39.3.7.0");var subQ1=sQuery(id+"F0.wireOp",EDGE,"E33");var subQ2=makeQuery(id+"F0.imprint","INTERSECT",VERTEX,{"derivedFrom":[subQ1,subQ0]});Q28=makeQuery(id+"F0.imprint","IMPRINT",FACE,{"disambiguationData":[TD([[makeQuery(id+"F0.imprint","IMPRINT",EDGE,{"disambiguationData":[TD([[subQ2,-1.0]])],"derivedFrom":subQ1}),1.0]])]});}
            var Q29;
            {var subQ0=sQuery(id+"F0.wireOp",EDGE,"E39.0.6.0");var subQ1=sQuery(id+"F0.wireOp",EDGE,"E33");var subQ2=makeQuery(id+"F0.imprint","INTERSECT",VERTEX,{"derivedFrom":[subQ1,subQ0]});Q29=makeQuery(id+"F0.imprint","IMPRINT",FACE,{"disambiguationData":[TD([[makeQuery(id+"F0.imprint","IMPRINT",EDGE,{"disambiguationData":[TD([[subQ2,-1.0]])],"derivedFrom":subQ1}),1.0]])]});}
            var Q30;
            {var subQ0=sQuery(id+"F0.wireOp",EDGE,"E39.3.6.0");var subQ1=sQuery(id+"F0.wireOp",EDGE,"E33");var subQ2=makeQuery(id+"F0.imprint","INTERSECT",VERTEX,{"derivedFrom":[subQ1,subQ0]});Q30=makeQuery(id+"F0.imprint","IMPRINT",FACE,{"disambiguationData":[TD([[makeQuery(id+"F0.imprint","IMPRINT",EDGE,{"disambiguationData":[TD([[subQ2,-1.0]])],"derivedFrom":subQ1}),1.0]])]});}
            var Q31;
            {var subQ0=sQuery(id+"F0.wireOp",EDGE,"E39.0.5.0");var subQ1=sQuery(id+"F0.wireOp",EDGE,"E33");var subQ2=makeQuery(id+"F0.imprint","INTERSECT",VERTEX,{"derivedFrom":[subQ1,subQ0]});Q31=makeQuery(id+"F0.imprint","IMPRINT",FACE,{"disambiguationData":[TD([[makeQuery(id+"F0.imprint","IMPRINT",EDGE,{"disambiguationData":[TD([[subQ2,-1.0]])],"derivedFrom":subQ1}),1.0]])]});}
            var Q32;
            {var subQ0=sQuery(id+"F0.wireOp",EDGE,"E39.3.5.0");var subQ1=sQuery(id+"F0.wireOp",EDGE,"E33");var subQ2=makeQuery(id+"F0.imprint","INTERSECT",VERTEX,{"derivedFrom":[subQ1,subQ0]});Q32=makeQuery(id+"F0.imprint","IMPRINT",FACE,{"disambiguationData":[TD([[makeQuery(id+"F0.imprint","IMPRINT",EDGE,{"disambiguationData":[TD([[subQ2,-1.0]])],"derivedFrom":subQ1}),1.0]])]});}
            var Q33;
            {var subQ0=sQuery(id+"F0.wireOp",EDGE,"E39.0.4.0");var subQ1=sQuery(id+"F0.wireOp",EDGE,"E33");var subQ2=makeQuery(id+"F0.imprint","INTERSECT",VERTEX,{"derivedFrom":[subQ1,subQ0]});Q33=makeQuery(id+"F0.imprint","IMPRINT",FACE,{"disambiguationData":[TD([[makeQuery(id+"F0.imprint","IMPRINT",EDGE,{"disambiguationData":[TD([[subQ2,-1.0]])],"derivedFrom":subQ1}),1.0]])]});}
            var Q34;
            {var subQ0=sQuery(id+"F0.wireOp",EDGE,"E39.3.4.0");var subQ1=sQuery(id+"F0.wireOp",EDGE,"E33");var subQ2=makeQuery(id+"F0.imprint","INTERSECT",VERTEX,{"derivedFrom":[subQ1,subQ0]});Q34=makeQuery(id+"F0.imprint","IMPRINT",FACE,{"disambiguationData":[TD([[makeQuery(id+"F0.imprint","IMPRINT",EDGE,{"disambiguationData":[TD([[subQ2,-1.0]])],"derivedFrom":subQ1}),1.0]])]});}
            var Q35;
            {var subQ0=sQuery(id+"F0.wireOp",EDGE,"E39.0.3.0");var subQ1=sQuery(id+"F0.wireOp",EDGE,"E33");var subQ2=makeQuery(id+"F0.imprint","INTERSECT",VERTEX,{"derivedFrom":[subQ1,subQ0]});Q35=makeQuery(id+"F0.imprint","IMPRINT",FACE,{"disambiguationData":[TD([[makeQuery(id+"F0.imprint","IMPRINT",EDGE,{"disambiguationData":[TD([[subQ2,-1.0]])],"derivedFrom":subQ1}),1.0]])]});}
            var Q36;
            {var subQ0=sQuery(id+"F0.wireOp",EDGE,"E39.3.3.0");var subQ1=sQuery(id+"F0.wireOp",EDGE,"E33");var subQ2=makeQuery(id+"F0.imprint","INTERSECT",VERTEX,{"derivedFrom":[subQ1,subQ0]});Q36=makeQuery(id+"F0.imprint","IMPRINT",FACE,{"disambiguationData":[TD([[makeQuery(id+"F0.imprint","IMPRINT",EDGE,{"disambiguationData":[TD([[subQ2,-1.0]])],"derivedFrom":subQ1}),1.0]])]});}
            var Q37;
            {var subQ0=sQuery(id+"F0.wireOp",EDGE,"E38.2.0.0");var subQ1=sQuery(id+"F0.wireOp",EDGE,"E33");var subQ2=makeQuery(id+"F0.imprint","INTERSECT",VERTEX,{"derivedFrom":[subQ1,subQ0]});Q37=makeQuery(id+"F0.imprint","IMPRINT",FACE,{"disambiguationData":[TD([[makeQuery(id+"F0.imprint","IMPRINT",EDGE,{"disambiguationData":[TD([[subQ2,-1.0]])],"derivedFrom":subQ1}),1.0]])]});}
            var Q38;
            {var subQ0=sQuery(id+"F0.wireOp",EDGE,"E38.2.0.1");var subQ1=sQuery(id+"F0.wireOp",EDGE,"E33");var subQ2=makeQuery(id+"F0.imprint","INTERSECT",VERTEX,{"derivedFrom":[subQ1,subQ0]});Q38=makeQuery(id+"F0.imprint","IMPRINT",FACE,{"disambiguationData":[TD([[makeQuery(id+"F0.imprint","IMPRINT",EDGE,{"disambiguationData":[TD([[subQ2,-1.0]])],"derivedFrom":subQ1}),1.0]])]});}
            var Q39;
            {var subQ0=sQuery(id+"F0.wireOp",EDGE,"E38.1.0.0");var subQ1=sQuery(id+"F0.wireOp",EDGE,"E33");var subQ2=makeQuery(id+"F0.imprint","INTERSECT",VERTEX,{"derivedFrom":[subQ1,subQ0]});Q39=makeQuery(id+"F0.imprint","IMPRINT",FACE,{"disambiguationData":[TD([[makeQuery(id+"F0.imprint","IMPRINT",EDGE,{"disambiguationData":[TD([[subQ2,-1.0]])],"derivedFrom":subQ1}),1.0]])]});}
            var Q40;
            {var subQ0=sQuery(id+"F0.wireOp",EDGE,"E38.1.0.1");var subQ1=sQuery(id+"F0.wireOp",EDGE,"E33");var subQ2=makeQuery(id+"F0.imprint","INTERSECT",VERTEX,{"derivedFrom":[subQ1,subQ0]});Q40=makeQuery(id+"F0.imprint","IMPRINT",FACE,{"disambiguationData":[TD([[makeQuery(id+"F0.imprint","IMPRINT",EDGE,{"disambiguationData":[TD([[subQ2,-1.0]])],"derivedFrom":subQ1}),1.0]])]});}
            var Q41;
            {var subQ0=sQuery(id+"F0.wireOp",EDGE,"E37.right");var subQ1=sQuery(id+"F0.wireOp",EDGE,"E33");var subQ2=makeQuery(id+"F0.imprint","INTERSECT",VERTEX,{"derivedFrom":[subQ1,subQ0]});Q41=makeQuery(id+"F0.imprint","IMPRINT",FACE,{"disambiguationData":[TD([[makeQuery(id+"F0.imprint","IMPRINT",EDGE,{"disambiguationData":[TD([[subQ2,-1.0]])],"derivedFrom":subQ1}),1.0]])]});}
            var Q42;
            {var subQ0=sQuery(id+"F0.wireOp",EDGE,"E37.bottom");Q42=makeQuery(id+"F0.imprint","IMPRINT",FACE,{"disambiguationData":[TD([[makeQuery(id+"F0.imprint","IMPRINT",EDGE,{"derivedFrom":subQ0}),1.0]])]});}
            var Q43;
            {var subQ1=sQuery(id+"F0.wireOp",EDGE,"E36");var subQ3=sQuery(id+"F0.wireOp",EDGE,"E38.1.0.1");var subQ4=makeQuery(id+"F0.imprint","INTERSECT",VERTEX,{"derivedFrom":[subQ1,subQ3]});Q43=makeQuery(id+"F0.imprint","IMPRINT",FACE,{"disambiguationData":[TD([[makeQuery(id+"F0.imprint","IMPRINT",EDGE,{"disambiguationData":[TD([[subQ4,-1.0]])],"derivedFrom":subQ3}),1.0]])]});}
            var Q44;
            {var subQ0=sQuery(id+"F0.wireOp",EDGE,"E38.1.0.0");var subQ1=sQuery(id+"F0.wireOp",EDGE,"E36");var subQ2=makeQuery(id+"F0.imprint","INTERSECT",VERTEX,{"derivedFrom":[subQ1,subQ0]});Q44=makeQuery(id+"F0.imprint","IMPRINT",FACE,{"disambiguationData":[TD([[makeQuery(id+"F0.imprint","IMPRINT",EDGE,{"disambiguationData":[TD([[subQ2,1.0]])],"derivedFrom":subQ1}),1.0]])]});}
            var Q45;
            {var subQ0=sQuery(id+"F0.wireOp",EDGE,"E38.1.0.0");var subQ1=sQuery(id+"F0.wireOp",EDGE,"E36");var subQ2=makeQuery(id+"F0.imprint","INTERSECT",VERTEX,{"derivedFrom":[subQ1,subQ0]});Q45=makeQuery(id+"F0.imprint","IMPRINT",FACE,{"disambiguationData":[TD([[makeQuery(id+"F0.imprint","IMPRINT",EDGE,{"disambiguationData":[TD([[subQ2,-1.0]])],"derivedFrom":subQ1}),1.0]])]});}
            var Q46;
            {var subQ0=sQuery(id+"F0.wireOp",EDGE,"E38.2.0.0");var subQ1=sQuery(id+"F0.wireOp",EDGE,"E36");var subQ2=makeQuery(id+"F0.imprint","INTERSECT",VERTEX,{"derivedFrom":[subQ1,subQ0]});Q46=makeQuery(id+"F0.imprint","IMPRINT",FACE,{"disambiguationData":[TD([[makeQuery(id+"F0.imprint","IMPRINT",EDGE,{"disambiguationData":[TD([[subQ2,1.0]])],"derivedFrom":subQ1}),1.0]])]});}
            var Q47;
            {var subQ0=sQuery(id+"F0.wireOp",EDGE,"E38.2.0.0");var subQ1=sQuery(id+"F0.wireOp",EDGE,"E36");var subQ2=makeQuery(id+"F0.imprint","INTERSECT",VERTEX,{"derivedFrom":[subQ1,subQ0]});Q47=makeQuery(id+"F0.imprint","IMPRINT",FACE,{"disambiguationData":[TD([[makeQuery(id+"F0.imprint","IMPRINT",EDGE,{"disambiguationData":[TD([[subQ2,-1.0]])],"derivedFrom":subQ1}),1.0]])]});}
            var Q48;
            {var subQ0=sQuery(id+"F0.wireOp",EDGE,"E39.0.3.0");var subQ1=sQuery(id+"F0.wireOp",EDGE,"E36");var subQ2=makeQuery(id+"F0.imprint","INTERSECT",VERTEX,{"derivedFrom":[subQ1,subQ0]});Q48=makeQuery(id+"F0.imprint","IMPRINT",FACE,{"disambiguationData":[TD([[makeQuery(id+"F0.imprint","IMPRINT",EDGE,{"disambiguationData":[TD([[subQ2,1.0]])],"derivedFrom":subQ1}),1.0]])]});}
            var Q49;
            {var subQ0=sQuery(id+"F0.wireOp",EDGE,"E39.0.3.0");var subQ1=sQuery(id+"F0.wireOp",EDGE,"E36");var subQ2=makeQuery(id+"F0.imprint","INTERSECT",VERTEX,{"derivedFrom":[subQ1,subQ0]});Q49=makeQuery(id+"F0.imprint","IMPRINT",FACE,{"disambiguationData":[TD([[makeQuery(id+"F0.imprint","IMPRINT",EDGE,{"disambiguationData":[TD([[subQ2,-1.0]])],"derivedFrom":subQ1}),1.0]])]});}
            var Q50;
            {var subQ0=sQuery(id+"F0.wireOp",EDGE,"E39.0.4.0");var subQ1=sQuery(id+"F0.wireOp",EDGE,"E36");var subQ2=makeQuery(id+"F0.imprint","INTERSECT",VERTEX,{"derivedFrom":[subQ1,subQ0]});Q50=makeQuery(id+"F0.imprint","IMPRINT",FACE,{"disambiguationData":[TD([[makeQuery(id+"F0.imprint","IMPRINT",EDGE,{"disambiguationData":[TD([[subQ2,1.0]])],"derivedFrom":subQ1}),1.0]])]});}
            var Q51;
            {var subQ0=sQuery(id+"F0.wireOp",EDGE,"E39.0.4.0");var subQ1=sQuery(id+"F0.wireOp",EDGE,"E36");var subQ2=makeQuery(id+"F0.imprint","INTERSECT",VERTEX,{"derivedFrom":[subQ1,subQ0]});Q51=makeQuery(id+"F0.imprint","IMPRINT",FACE,{"disambiguationData":[TD([[makeQuery(id+"F0.imprint","IMPRINT",EDGE,{"disambiguationData":[TD([[subQ2,-1.0]])],"derivedFrom":subQ1}),1.0]])]});}
            var Q52;
            {var subQ0=sQuery(id+"F0.wireOp",EDGE,"E39.0.5.0");var subQ1=sQuery(id+"F0.wireOp",EDGE,"E36");var subQ2=makeQuery(id+"F0.imprint","INTERSECT",VERTEX,{"derivedFrom":[subQ1,subQ0]});Q52=makeQuery(id+"F0.imprint","IMPRINT",FACE,{"disambiguationData":[TD([[makeQuery(id+"F0.imprint","IMPRINT",EDGE,{"disambiguationData":[TD([[subQ2,1.0]])],"derivedFrom":subQ1}),1.0]])]});}
            var Q53;
            {var subQ0=sQuery(id+"F0.wireOp",EDGE,"E39.0.5.0");var subQ1=sQuery(id+"F0.wireOp",EDGE,"E36");var subQ2=makeQuery(id+"F0.imprint","INTERSECT",VERTEX,{"derivedFrom":[subQ1,subQ0]});Q53=makeQuery(id+"F0.imprint","IMPRINT",FACE,{"disambiguationData":[TD([[makeQuery(id+"F0.imprint","IMPRINT",EDGE,{"disambiguationData":[TD([[subQ2,-1.0]])],"derivedFrom":subQ1}),1.0]])]});}
            var Q54;
            {var subQ0=sQuery(id+"F0.wireOp",EDGE,"E39.0.6.0");var subQ1=sQuery(id+"F0.wireOp",EDGE,"E36");var subQ2=makeQuery(id+"F0.imprint","INTERSECT",VERTEX,{"derivedFrom":[subQ1,subQ0]});Q54=makeQuery(id+"F0.imprint","IMPRINT",FACE,{"disambiguationData":[TD([[makeQuery(id+"F0.imprint","IMPRINT",EDGE,{"disambiguationData":[TD([[subQ2,1.0]])],"derivedFrom":subQ1}),1.0]])]});}
            var Q55;
            {var subQ0=sQuery(id+"F0.wireOp",EDGE,"E39.0.6.0");var subQ1=sQuery(id+"F0.wireOp",EDGE,"E36");var subQ2=makeQuery(id+"F0.imprint","INTERSECT",VERTEX,{"derivedFrom":[subQ1,subQ0]});Q55=makeQuery(id+"F0.imprint","IMPRINT",FACE,{"disambiguationData":[TD([[makeQuery(id+"F0.imprint","IMPRINT",EDGE,{"disambiguationData":[TD([[subQ2,-1.0]])],"derivedFrom":subQ1}),1.0]])]});}
            var Q56;
            {var subQ0=sQuery(id+"F0.wireOp",EDGE,"E39.0.7.0");var subQ1=sQuery(id+"F0.wireOp",EDGE,"E36");var subQ2=makeQuery(id+"F0.imprint","INTERSECT",VERTEX,{"derivedFrom":[subQ1,subQ0]});Q56=makeQuery(id+"F0.imprint","IMPRINT",FACE,{"disambiguationData":[TD([[makeQuery(id+"F0.imprint","IMPRINT",EDGE,{"disambiguationData":[TD([[subQ2,1.0]])],"derivedFrom":subQ1}),1.0]])]});}
            var Q57;
            {var subQ0=sQuery(id+"F0.wireOp",EDGE,"E39.0.9.0");var subQ1=sQuery(id+"F0.wireOp",EDGE,"E36");var subQ2=makeQuery(id+"F0.imprint","INTERSECT",VERTEX,{"derivedFrom":[subQ1,subQ0]});Q57=makeQuery(id+"F0.imprint","IMPRINT",FACE,{"disambiguationData":[TD([[makeQuery(id+"F0.imprint","IMPRINT",EDGE,{"disambiguationData":[TD([[subQ2,1.0]])],"derivedFrom":subQ1}),1.0]])]});}
            var Q58;
            {var subQ0=sQuery(id+"F0.wireOp",EDGE,"E39.0.8.0");var subQ1=sQuery(id+"F0.wireOp",EDGE,"E36");var subQ2=makeQuery(id+"F0.imprint","INTERSECT",VERTEX,{"derivedFrom":[subQ1,subQ0]});Q58=makeQuery(id+"F0.imprint","IMPRINT",FACE,{"disambiguationData":[TD([[makeQuery(id+"F0.imprint","IMPRINT",EDGE,{"disambiguationData":[TD([[subQ2,-1.0]])],"derivedFrom":subQ1}),1.0]])]});}
            var Q59;
            {var subQ0=sQuery(id+"F0.wireOp",EDGE,"E39.0.8.0");var subQ1=sQuery(id+"F0.wireOp",EDGE,"E36");var subQ2=makeQuery(id+"F0.imprint","INTERSECT",VERTEX,{"derivedFrom":[subQ1,subQ0]});Q59=makeQuery(id+"F0.imprint","IMPRINT",FACE,{"disambiguationData":[TD([[makeQuery(id+"F0.imprint","IMPRINT",EDGE,{"disambiguationData":[TD([[subQ2,1.0]])],"derivedFrom":subQ1}),1.0]])]});}
            var Q60;
            {var subQ0=sQuery(id+"F0.wireOp",EDGE,"E39.0.7.0");var subQ1=sQuery(id+"F0.wireOp",EDGE,"E36");var subQ2=makeQuery(id+"F0.imprint","INTERSECT",VERTEX,{"derivedFrom":[subQ1,subQ0]});Q60=makeQuery(id+"F0.imprint","IMPRINT",FACE,{"disambiguationData":[TD([[makeQuery(id+"F0.imprint","IMPRINT",EDGE,{"disambiguationData":[TD([[subQ2,-1.0]])],"derivedFrom":subQ1}),1.0]])]});}
            extrude(context, id + "F10", {"entities" : qUnion([Q0, Q1, Q2, Q3, Q4, Q5, Q6, Q7, Q8, Q9, Q10, Q11, Q12, Q13, Q14, Q15, Q16, Q17, Q18, Q19, Q20, Q21, Q22, Q23, Q24, Q25, Q26, Q27, Q28, Q29, Q30, Q31, Q32, Q33, Q34, Q35, Q36, Q37, Q38, Q39, Q40, Q41, Q42, Q43, Q44, Q45, Q46, Q47, Q48, Q49, Q50, Q51, Q52, Q53, Q54, Q55, Q56, Q57, Q58, Q59, Q60]), "operationType" : NewBodyOperationType.ADD, "depth" : 8 * mm, "offsetDistance" : 25 * mm});
        }
        {
            var Q0;
            {var subQ0=sQuery(id+"F0.wireOp",EDGE,"E40.bottom");var subQ1=sQuery(id+"F0.wireOp",EDGE,"E37.left");var subQ2=makeQuery(id+"F0.imprint","INTERSECT",VERTEX,{"derivedFrom":[subQ1,subQ0]});Q0=makeQuery(id+"F0.imprint","IMPRINT",FACE,{"disambiguationData":[TD([[makeQuery(id+"F0.imprint","IMPRINT",EDGE,{"disambiguationData":[TD([[subQ2,-1.0]])],"derivedFrom":subQ1}),-1.0]])]});}
            var Q1;
            {var subQ0=sQuery(id+"F0.wireOp",EDGE,"E40.bottom");var subQ1=sQuery(id+"F0.wireOp",EDGE,"E38.1.0.0");var subQ2=makeQuery(id+"F0.imprint","INTERSECT",VERTEX,{"derivedFrom":[subQ1,subQ0]});Q1=makeQuery(id+"F0.imprint","IMPRINT",FACE,{"disambiguationData":[TD([[makeQuery(id+"F0.imprint","IMPRINT",EDGE,{"disambiguationData":[TD([[subQ2,-1.0]])],"derivedFrom":subQ1}),1.0]])]});}
            var Q2;
            {var subQ0=sQuery(id+"F0.wireOp",EDGE,"E40.bottom");var subQ1=sQuery(id+"F0.wireOp",EDGE,"E38.2.0.0");var subQ2=makeQuery(id+"F0.imprint","INTERSECT",VERTEX,{"derivedFrom":[subQ1,subQ0]});Q2=makeQuery(id+"F0.imprint","IMPRINT",FACE,{"disambiguationData":[TD([[makeQuery(id+"F0.imprint","IMPRINT",EDGE,{"disambiguationData":[TD([[subQ2,-1.0]])],"derivedFrom":subQ1}),1.0]])]});}
            var Q3;
            {var subQ0=sQuery(id+"F0.wireOp",EDGE,"E40.bottom");var subQ1=sQuery(id+"F0.wireOp",EDGE,"E39.0.3.0");var subQ2=makeQuery(id+"F0.imprint","INTERSECT",VERTEX,{"derivedFrom":[subQ1,subQ0]});Q3=makeQuery(id+"F0.imprint","IMPRINT",FACE,{"disambiguationData":[TD([[makeQuery(id+"F0.imprint","IMPRINT",EDGE,{"disambiguationData":[TD([[subQ2,-1.0]])],"derivedFrom":subQ1}),1.0]])]});}
            var Q4;
            {var subQ0=sQuery(id+"F0.wireOp",EDGE,"E40.bottom");var subQ1=sQuery(id+"F0.wireOp",EDGE,"E39.0.4.0");var subQ2=makeQuery(id+"F0.imprint","INTERSECT",VERTEX,{"derivedFrom":[subQ1,subQ0]});Q4=makeQuery(id+"F0.imprint","IMPRINT",FACE,{"disambiguationData":[TD([[makeQuery(id+"F0.imprint","IMPRINT",EDGE,{"disambiguationData":[TD([[subQ2,-1.0]])],"derivedFrom":subQ1}),1.0]])]});}
            var Q5;
            {var subQ0=sQuery(id+"F0.wireOp",EDGE,"E40.bottom");var subQ1=sQuery(id+"F0.wireOp",EDGE,"E39.0.5.0");var subQ2=makeQuery(id+"F0.imprint","INTERSECT",VERTEX,{"derivedFrom":[subQ1,subQ0]});Q5=makeQuery(id+"F0.imprint","IMPRINT",FACE,{"disambiguationData":[TD([[makeQuery(id+"F0.imprint","IMPRINT",EDGE,{"disambiguationData":[TD([[subQ2,-1.0]])],"derivedFrom":subQ1}),1.0]])]});}
            var Q6;
            {var subQ0=sQuery(id+"F0.wireOp",EDGE,"E40.bottom");var subQ1=sQuery(id+"F0.wireOp",EDGE,"E39.0.6.0");var subQ2=makeQuery(id+"F0.imprint","INTERSECT",VERTEX,{"derivedFrom":[subQ1,subQ0]});Q6=makeQuery(id+"F0.imprint","IMPRINT",FACE,{"disambiguationData":[TD([[makeQuery(id+"F0.imprint","IMPRINT",EDGE,{"disambiguationData":[TD([[subQ2,-1.0]])],"derivedFrom":subQ1}),1.0]])]});}
            var Q7;
            {var subQ0=sQuery(id+"F0.wireOp",EDGE,"E40.bottom");var subQ1=sQuery(id+"F0.wireOp",EDGE,"E39.0.7.0");var subQ2=makeQuery(id+"F0.imprint","INTERSECT",VERTEX,{"derivedFrom":[subQ1,subQ0]});Q7=makeQuery(id+"F0.imprint","IMPRINT",FACE,{"disambiguationData":[TD([[makeQuery(id+"F0.imprint","IMPRINT",EDGE,{"disambiguationData":[TD([[subQ2,-1.0]])],"derivedFrom":subQ1}),1.0]])]});}
            var Q8;
            {var subQ0=sQuery(id+"F0.wireOp",EDGE,"E40.bottom");var subQ1=sQuery(id+"F0.wireOp",EDGE,"E39.0.8.0");var subQ2=makeQuery(id+"F0.imprint","INTERSECT",VERTEX,{"derivedFrom":[subQ1,subQ0]});Q8=makeQuery(id+"F0.imprint","IMPRINT",FACE,{"disambiguationData":[TD([[makeQuery(id+"F0.imprint","IMPRINT",EDGE,{"disambiguationData":[TD([[subQ2,-1.0]])],"derivedFrom":subQ1}),1.0]])]});}
            var Q9;
            {var subQ0=sQuery(id+"F0.wireOp",EDGE,"E40.bottom");var subQ1=sQuery(id+"F0.wireOp",EDGE,"E39.0.9.0");var subQ2=makeQuery(id+"F0.imprint","INTERSECT",VERTEX,{"derivedFrom":[subQ1,subQ0]});Q9=makeQuery(id+"F0.imprint","IMPRINT",FACE,{"disambiguationData":[TD([[makeQuery(id+"F0.imprint","IMPRINT",EDGE,{"disambiguationData":[TD([[subQ2,-1.0]])],"derivedFrom":subQ1}),1.0]])]});}
            extrude(context, id + "F11", {"entities" : qUnion([Q0, Q1, Q2, Q3, Q4, Q5, Q6, Q7, Q8, Q9]), "operationType" : NewBodyOperationType.REMOVE, "depth" : 25 * mm, "offsetDistance" : 25 * mm});
        }
    });
